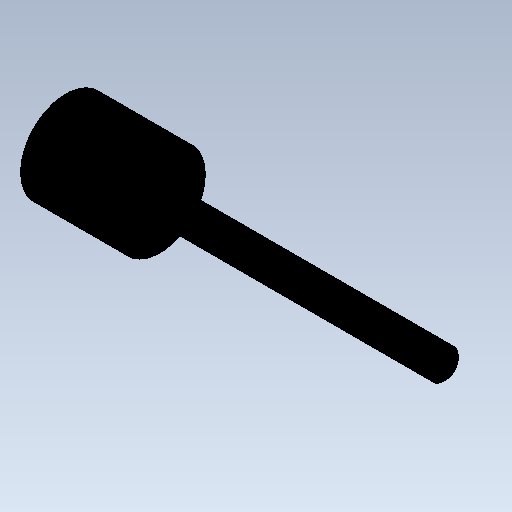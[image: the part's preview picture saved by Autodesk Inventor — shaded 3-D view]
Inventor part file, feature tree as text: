
AUTODESK INVENTOR PART (.ipt)
format: ipt  version: 2020 (Build 240168000, 168)  size: 140,288 bytes
history: native  units: mm (DEFAULTED — no unit token found)
features: other x70, revolve x3, sketch x3
ambient origin geometry x8: Origin, YZ Plane, XZ Plane, XY Plane, X Axis, Y Axis, Z Axis, Center Point
bodies: Solid1 (feature_tree)
feature tree (76):
  revolve  "Revolution1"  Angle=360.0deg
  revolve  "Revolution2"  [1 undecoded]
  revolve  "Revolution3"  [1 undecoded]
  other  "dia1_XY"
  other  "dia1_YZ"
  other  "dia1_ZX"
  other  "dia1_X"
  other  "dia1_Y"
  other  "dia1_Z"
  other  "dia1_Center"
  other  "dia12_XY"
  other  "dia12_YZ"
  other  "dia12_ZX"
  other  "dia12_X"
  other  "dia12_Y"
  other  "dia12_Z"
  other  "dia12_Center"
  other  "dia2_XY"
  other  "dia2_YZ"
  other  "dia2_ZX"
  other  "dia2_X"
  other  "dia2_Y"
  other  "dia2_Z"
  other  "dia2_Center"
  other  "dia22_XY"
  other  "dia22_YZ"
  other  "dia22_ZX"
  other  "dia22_X"
  other  "dia22_Y"
  other  "dia22_Z"
  other  "dia22_Center"
  other  "rl1_XY"
  other  "rl1_YZ"
  other  "rl1_ZX"
  other  "rl1_X"
  other  "rl1_Y"
  other  "rl1_Z"
  other  "rl1_Center"
  other  "rl2_XY"
  other  "rl2_YZ"
  other  "rl2_ZX"
  other  "rl2_X"
  other  "rl2_Y"
  other  "rl2_Z"
  other  "rl2_Center"
  other  "rod_cp_XY"
  other  "rod_cp_YZ"
  other  "rod_cp_ZX"
  other  "rod_cp_X"
  other  "rod_cp_Y"
  other  "rod_cp_Z"
  other  "rod_cp_Center"
  other  "thd1_XY"
  other  "thd1_YZ"
  other  "thd1_ZX"
  other  "thd1_X"
  other  "thd1_Y"
  other  "thd1_Z"
  other  "thd1_Center"
  other  "thd2_XY"
  other  "thd2_YZ"
  other  "thd2_ZX"
  other  "thd2_X"
  other  "thd2_Y"
  other  "thd2_Z"
  other  "thd2_Center"
  other  "to_rod_clevis_XY"
  other  "to_rod_clevis_YZ"
  other  "to_rod_clevis_ZX"
  other  "to_rod_clevis_X"
  other  "to_rod_clevis_Y"
  other  "to_rod_clevis_Z"
  other  "to_rod_clevis_Center"
  sketch  "Sketch_1"  dims[d0=360.0deg d1=360.0deg]
  sketch  "Sketch_3"  dims[d2=360.0deg]
  sketch  "Sketch_30"  dims[d3=0.0mm d4=0.0mm d5=0.0mm d6=0.0mm d7=0.0mm]
note: 2 required parameter values undecoded (feature->parameter linkage not recoverable at this tier; creation-order binding heuristic only, values carry confidence <= 0.55)
